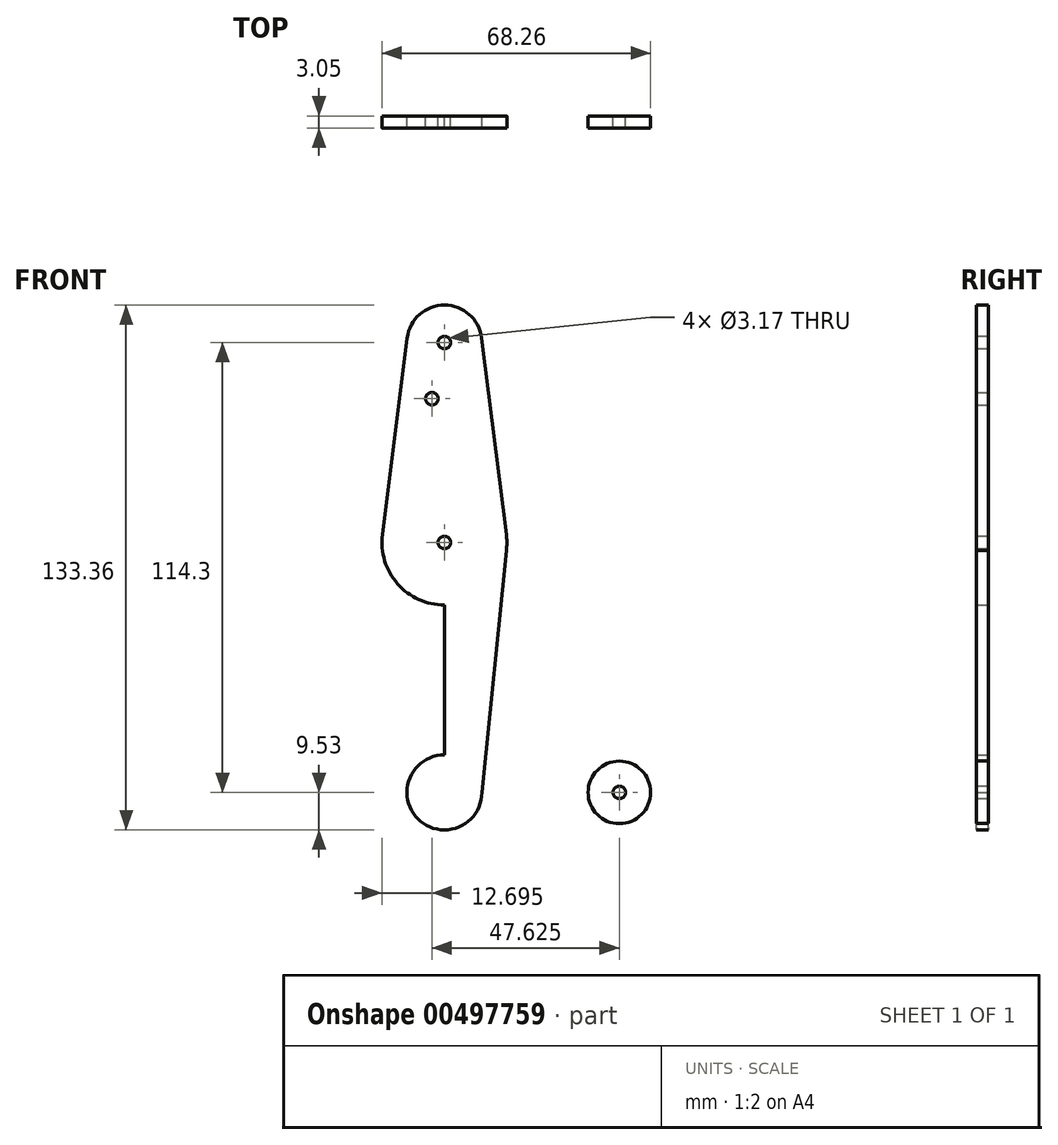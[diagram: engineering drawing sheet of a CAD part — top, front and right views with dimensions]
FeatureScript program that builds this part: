
annotation { "Feature Type Name" : "Feature", "Feature Type Description" : "" }
export const myFeature = defineFeature(function(context is Context, id is Id, definition is map)
    precondition{}
    {
        {
            var Q0;
            Q0=qCreatedBy(makeId("Front.planeOp"),FACE);
            var sketch = newSketch(context, id + "F0", { "sketchPlane" : qUnion([Q0])});
            skCircle(sketch, "E0", {"center": v(44.45, 0) * mm, "radius": 7.94 * mm});
            skCircle(sketch, "E1", {"center": v(0, 63.5) * mm, "radius": 15.88 * mm});
            skCircle(sketch, "E2", {"center": v(0, 114.3) * mm, "radius": 9.53 * mm});
            skLineSegment(sketch, "E3", {"start": v(0, 114.3) * mm, "end": v(0, 0) * mm});
            skLineSegment(sketch, "E4", {"start": v(0, 0) * mm, "end": v(44.45, 0) * mm});
            skLineSegment(sketch, "E5", {"start": v(-9.45, 115.5) * mm, "end": v(-15.75, 65.48) * mm});
            skLineSegment(sketch, "E6", {"start": v(9.45, 115.5) * mm, "end": v(15.75, 65.48) * mm});
            skCircle(sketch, "E7", {"center": v(-3.17, 100.03) * mm, "radius": 1.59 * mm});
            skCircle(sketch, "E8", {"center": v(0, 63.5) * mm, "radius": 1.59 * mm});
            skCircle(sketch, "E9", {"center": v(44.45, 0) * mm, "radius": 1.59 * mm});
            skCircle(sketch, "E10", {"center": v(0, 114.3) * mm, "radius": 1.59 * mm});
            skCircle(sketch, "E11", {"center": v(0, 0) * mm, "radius": 9.53 * mm});
            skLineSegment(sketch, "E12", {"start": v(-15.75, 61.52) * mm, "end": v(-9.57, 0) * mm});
            skLineSegment(sketch, "E13", {"start": v(15.75, 61.52) * mm, "end": v(9.57, 0) * mm});
            skLineSegment(sketch, "E14", {"start": v(0, 9.53) * mm, "end": v(44.45, 7.94) * mm});
            skLineSegment(sketch, "E15", {"start": v(0, -9.53) * mm, "end": v(44.45, -7.94) * mm});
            skSolve(sketch);
        }
        {
            var Q0;
            Q0 = qSketchRegion(id + "F0", true);
            extrude(context, id + "F1", {"entities" : qUnion([Q0]), "depth" : 3.05 * mm});
        }
    });
